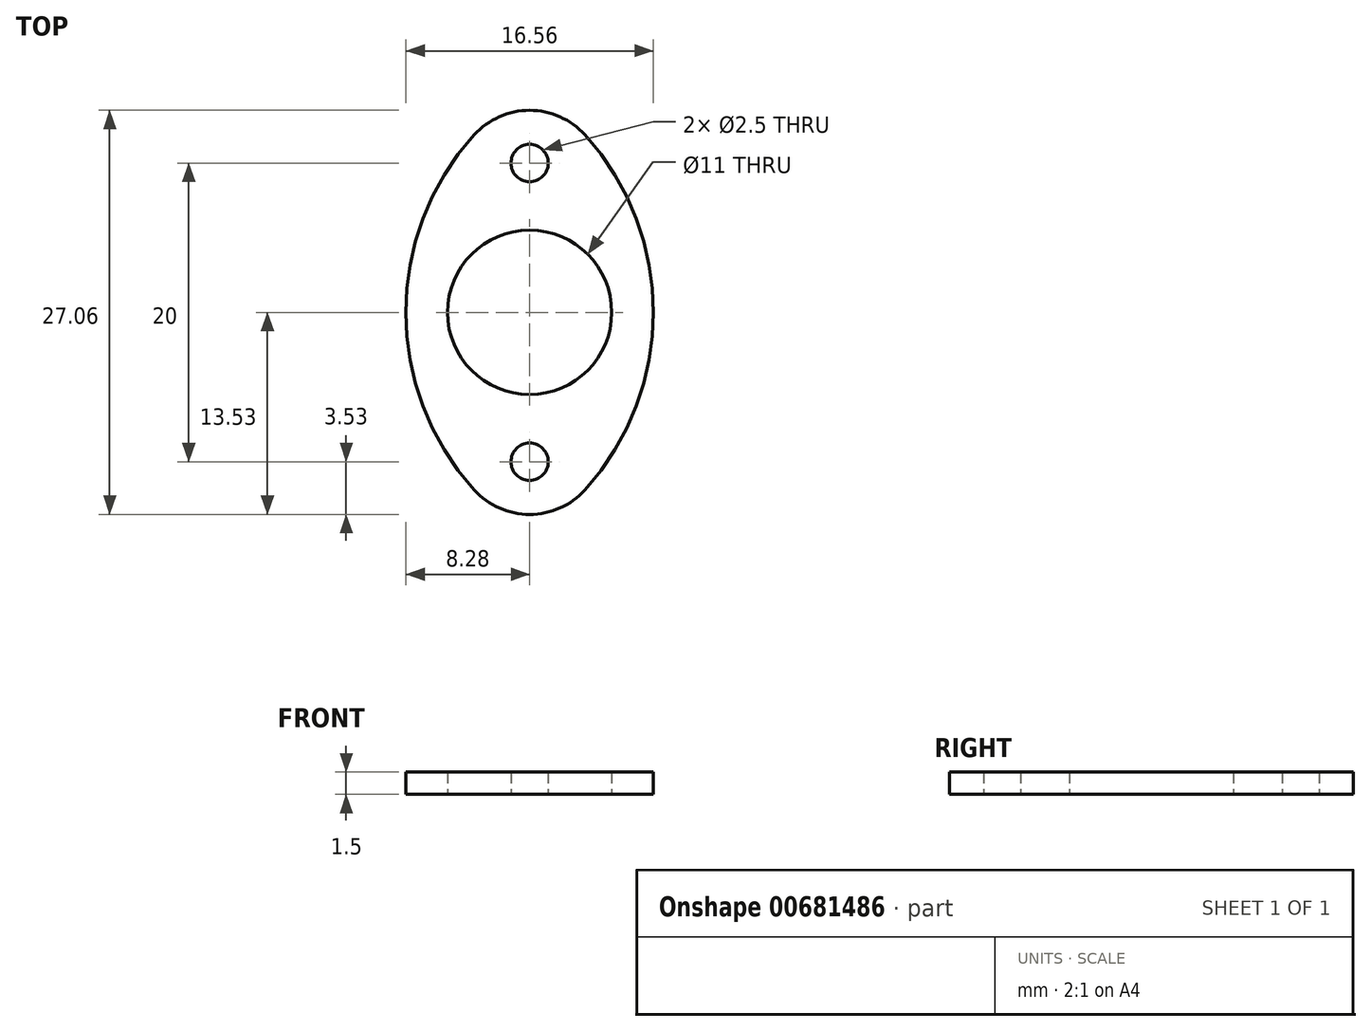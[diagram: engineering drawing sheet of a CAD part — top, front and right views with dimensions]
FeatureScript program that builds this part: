
annotation { "Feature Type Name" : "Feature", "Feature Type Description" : "" }
export const myFeature = defineFeature(function(context is Context, id is Id, definition is map)
    precondition{}
    {
        {
            var Q0;
            Q0=qCreatedBy(makeId("Top.planeOp"),FACE);
            var sketch = newSketch(context, id + "F0", { "sketchPlane" : qUnion([Q0])});
            skCircle(sketch, "E0", {"center": v(0, 0) * mm, "radius": 15 * mm});
            skCircle(sketch, "E1", {"center": v(0, 0) * mm, "radius": 5.5 * mm});
            skArc(sketch, "E2", {"start": v(0, -15) * mm, "mid": v(8.28, 0) * mm, "end": v(0, 15) * mm});
            skArc(sketch, "E3.MirrorCS", {"start": v(0, -15) * mm, "mid": v(-8.28, 0) * mm, "end": v(0, 15) * mm});
            skCircle(sketch, "E4", {"center": v(0, 10) * mm, "radius": 1.25 * mm});
            skCircle(sketch, "E5.MirrorC", {"center": v(0, -10) * mm, "radius": 1.25 * mm});
            skSolve(sketch);
        }
        {
            var Q0;
            Q0=makeQuery(id+"F0.imprint","IMPRINT",FACE,{"disambiguationData":[TD([[makeQuery(id+"F0.imprint","IMPRINT",EDGE,{"derivedFrom":sQuery(id+"F0.wireOp",EDGE,"E1")}),-1.0]])]});
            extrude(context, id + "F1", {"entities" : qUnion([Q0]), "depth" : 1.5 * mm, "offsetDistance" : 25 * mm});
        }
        {
            var Q0;
            {var subQ0=sQuery(id+"F0.wireOp",EDGE,"E3.MirrorCS");var subQ1=sQuery(id+"F0.wireOp",EDGE,"E2");var subQ2=sQuery(id+"F0.wireOp",EDGE,"E0");Q0=makeQuery(id+"F1.opExtrude","SWEPT_EDGE",EDGE,{"disambiguationData":[OSD([subQ2,subQ1,subQ0]),TDD([makeQuery(id+"F0.imprint","INTERSECT",VERTEX,{"disambiguationData":[OD(1.0)],"derivedFrom":[subQ2,subQ1,subQ0]})])]});}
            var Q1;
            {var subQ0=sQuery(id+"F0.wireOp",EDGE,"E3.MirrorCS");var subQ1=sQuery(id+"F0.wireOp",EDGE,"E2");var subQ2=sQuery(id+"F0.wireOp",EDGE,"E0");Q1=makeQuery(id+"F1.opExtrude","SWEPT_EDGE",EDGE,{"disambiguationData":[OSD([subQ2,subQ1,subQ0]),TDD([makeQuery(id+"F0.imprint","INTERSECT",VERTEX,{"disambiguationData":[OD(0.0)],"derivedFrom":[subQ2,subQ1,subQ0]})])]});}
            fillet(context, id + "F2", {"entities" : qUnion([Q0, Q1]), "radius" : 5 * mm, "tangentPropagation" : true, "allowEdgeOverflow" : false});
        }
    });
